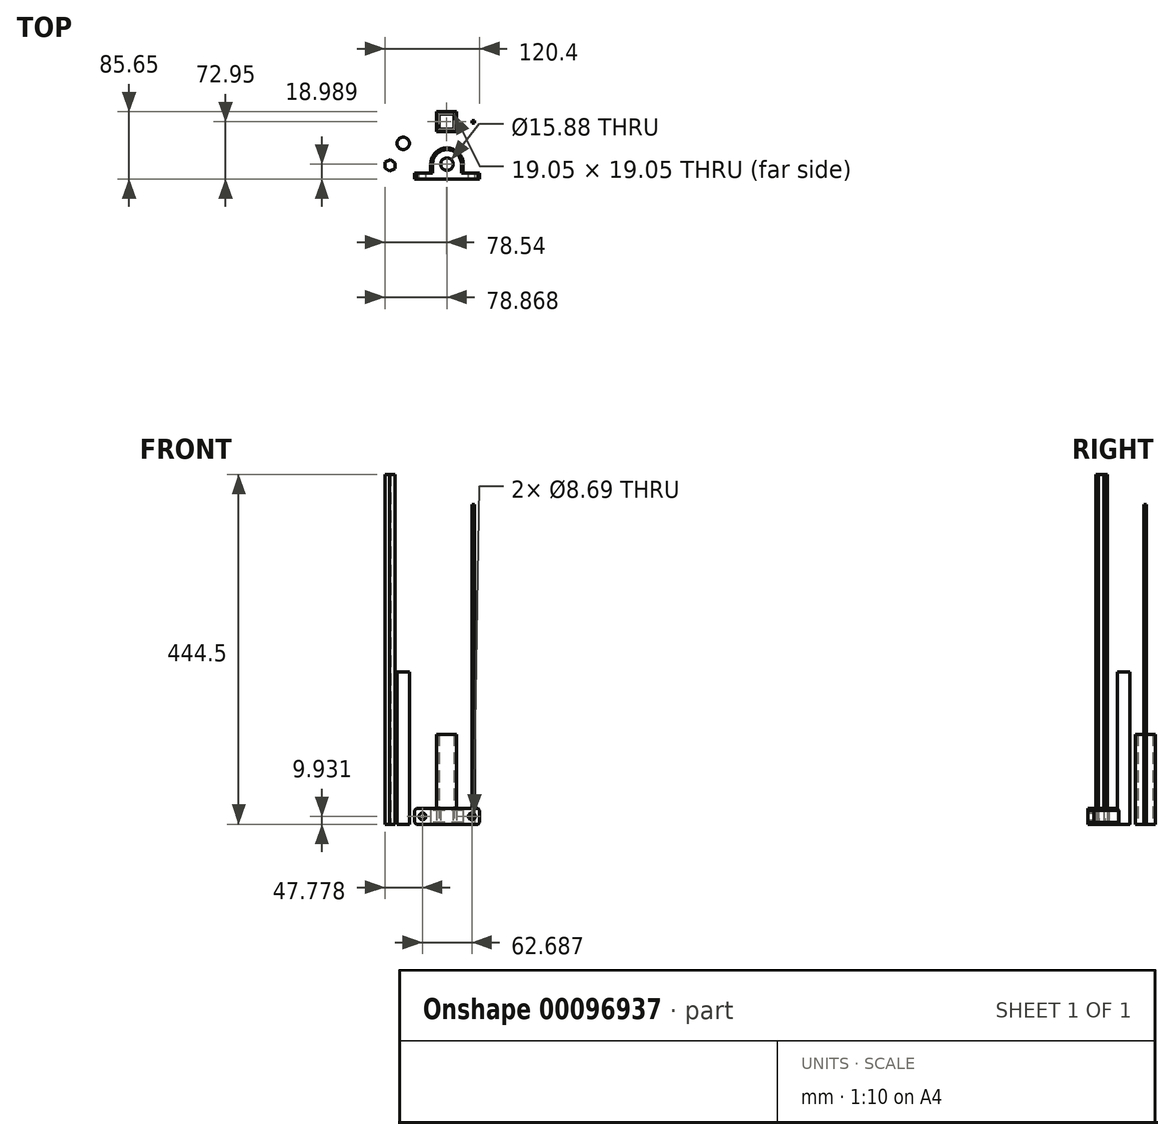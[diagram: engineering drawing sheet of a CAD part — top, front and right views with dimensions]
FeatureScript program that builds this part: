
annotation { "Feature Type Name" : "Feature", "Feature Type Description" : "" }
export const myFeature = defineFeature(function(context is Context, id is Id, definition is map)
    precondition{}
    {
        {
            var Q0;
            Q0=qCreatedBy(makeId("Top.planeOp"),FACE);
            var sketch = newSketch(context, id + "F0", { "sketchPlane" : qUnion([Q0])});
            skLineSegment(sketch, "E0.bottom", {"start": v(0, 0) * mm, "end": v(25.4, 0) * mm});
            skLineSegment(sketch, "E0.top", {"start": v(0, 25.4) * mm, "end": v(25.4, 25.4) * mm});
            skLineSegment(sketch, "E0.left", {"start": v(0, 0) * mm, "end": v(0, 25.4) * mm});
            skLineSegment(sketch, "E0.right", {"start": v(25.4, 0) * mm, "end": v(25.4, 25.4) * mm});
            skLineSegment(sketch, "E1.bottom", {"start": v(3.17, 3.18) * mm, "end": v(22.22, 3.18) * mm});
            skLineSegment(sketch, "E1.top", {"start": v(3.17, 22.23) * mm, "end": v(22.22, 22.23) * mm});
            skLineSegment(sketch, "E1.left", {"start": v(3.17, 3.18) * mm, "end": v(3.17, 22.23) * mm});
            skLineSegment(sketch, "E1.right", {"start": v(22.22, 3.18) * mm, "end": v(22.22, 22.23) * mm});
            skSolve(sketch);
        }
        {
            var Q0;
            Q0=makeQuery(id+"F0.imprint","IMPRINT",FACE,{"disambiguationData":[TD([[makeQuery(id+"F0.imprint","IMPRINT",EDGE,{"derivedFrom":sQuery(id+"F0.wireOp",EDGE,"E0.bottom")}),1.0]])]});
            extrude(context, id + "F1", {"entities" : qUnion([Q0]), "depth" : 114.3 * mm});
        }
        {
            var Q0;
            Q0=qCreatedBy(makeId("Top.planeOp"),FACE);
            var sketch = newSketch(context, id + "F2", { "sketchPlane" : qUnion([Q0])});
            skCircle(sketch, "E2", {"center": v(-42.54, -14.85) * mm, "radius": 7.94 * mm});
            skSolve(sketch);
        }
        {
            var Q0;
            Q0 = qSketchRegion(id + "F2", true);
            extrude(context, id + "F3", {"entities" : qUnion([Q0]), "depth" : 193.67 * mm});
        }
        {
            var Q0;
            Q0=qCreatedBy(makeId("Top.planeOp"),FACE);
            var sketch = newSketch(context, id + "F4", { "sketchPlane" : qUnion([Q0])});
            skLineSegment(sketch, "E3.bottom", {"start": v(-28, -60.25) * mm, "end": v(54.56, -60.25) * mm});
            skLineSegment(sketch, "E3.top", {"start": v(-28, -52.31) * mm, "end": v(-7.6, -52.31) * mm});
            skLineSegment(sketch, "E3.left", {"start": v(-28, -60.25) * mm, "end": v(-28, -52.31) * mm});
            skLineSegment(sketch, "E3.right", {"start": v(54.56, -60.25) * mm, "end": v(54.56, -52.31) * mm});
            skLineSegment(sketch, "E4.top", {"start": v(13.03, -20.62) * mm, "end": v(13.03, -20.62) * mm});
            skLineSegment(sketch, "E4.left", {"start": v(-7.6, -52.31) * mm, "end": v(-7.6, -41.26) * mm});
            skLineSegment(sketch, "E4.right", {"start": v(33.67, -52.31) * mm, "end": v(33.67, -41.26) * mm});
            skPoint(sketch, "E5.visualSharp", {"position": v(-7.6, -20.62) * mm});
            skArc(sketch, "E5.filletArc", {"start": v(13.03, -20.62) * mm, "mid": v(-1.57, -26.67) * mm, "end": v(-7.6, -41.26) * mm});
            skPoint(sketch, "E6.visualSharp", {"position": v(33.67, -20.62) * mm});
            skArc(sketch, "E6.filletArc", {"start": v(33.67, -41.26) * mm, "mid": v(27.62, -26.67) * mm, "end": v(13.03, -20.62) * mm});
            skCircle(sketch, "E7", {"center": v(13.03, -41.26) * mm, "radius": 7.94 * mm});
            skLineSegment(sketch, "E8.trimOffspring", {"start": v(33.67, -52.31) * mm, "end": v(54.56, -52.31) * mm});
            skSolve(sketch);
        }
        {
            var Q0;
            Q0=makeQuery(id+"F4.imprint","IMPRINT",FACE,{"disambiguationData":[TD([[makeQuery(id+"F4.imprint","IMPRINT",EDGE,{"derivedFrom":sQuery(id+"F4.wireOp",EDGE,"E3.bottom")}),1.0]])]});
            extrude(context, id + "F5", {"entities" : qUnion([Q0]), "depth" : 19.86 * mm});
        }
        {
            var Q0;
            Q0=makeQuery(id+"F5.opExtrude","CAP_EDGE",EDGE,{"disambiguationData":[OSD([sQuery(id+"F4.wireOp",EDGE,"E5.filletArc"),sQuery(id+"F4.wireOp",EDGE,"E6.filletArc")])],"isStart":false});
            var Q1;
            Q1=makeQuery(id+"F5.opExtrude","CAP_EDGE",EDGE,{"disambiguationData":[OSD([sQuery(id+"F4.wireOp",EDGE,"E4.left")])],"isStart":false});
            var Q2;
            Q2=makeQuery(id+"F5.opExtrude","CAP_EDGE",EDGE,{"disambiguationData":[OSD([sQuery(id+"F4.wireOp",EDGE,"E4.right")])],"isStart":false});
            var Q3;
            Q3=makeQuery(id+"F5.opExtrude","CAP_EDGE",EDGE,{"disambiguationData":[OSD([sQuery(id+"F4.wireOp",EDGE,"E4.right")])],"isStart":true});
            var Q4;
            Q4=makeQuery(id+"F5.opExtrude","CAP_EDGE",EDGE,{"disambiguationData":[OSD([sQuery(id+"F4.wireOp",EDGE,"E5.filletArc"),sQuery(id+"F4.wireOp",EDGE,"E6.filletArc")])],"isStart":true});
            var Q5;
            Q5=makeQuery(id+"F5.opExtrude","CAP_EDGE",EDGE,{"disambiguationData":[OSD([sQuery(id+"F4.wireOp",EDGE,"E4.left")])],"isStart":true});
            var Q6;
            Q6=makeQuery(id+"F5.opExtrude","CAP_EDGE",EDGE,{"disambiguationData":[OSD([sQuery(id+"F4.wireOp",EDGE,"E3.right")])],"isStart":true});
            var Q7;
            Q7=makeQuery(id+"F5.opExtrude","CAP_EDGE",EDGE,{"disambiguationData":[OSD([sQuery(id+"F4.wireOp",EDGE,"E3.right")])],"isStart":false});
            var Q8;
            Q8=makeQuery(id+"F5.opExtrude","CAP_EDGE",EDGE,{"disambiguationData":[OSD([sQuery(id+"F4.wireOp",EDGE,"E3.left")])],"isStart":true});
            var Q9;
            Q9=makeQuery(id+"F5.opExtrude","CAP_EDGE",EDGE,{"disambiguationData":[OSD([sQuery(id+"F4.wireOp",EDGE,"E3.left")])],"isStart":false});
            chamfer(context, id + "F6", {"entities" : qUnion([Q0, Q1, Q2, Q3, Q4, Q5, Q6, Q7, Q8, Q9]), "width" : 2.3 * mm, "tangentPropagation" : true});
        }
        {
            var Q0;
            Q0=makeQuery(id+"F5.opExtrude","SWEPT_FACE",FACE,{"disambiguationData":[OSD([sQuery(id+"F4.wireOp",EDGE,"E8.trimOffspring")])]});
            var sketch = newSketch(context, id + "F7", { "sketchPlane" : qUnion([Q0])});
            skCircle(sketch, "E9", {"center": v(18.06, 9.93) * mm, "radius": 4.34 * mm});
            skCircle(sketch, "E10", {"center": v(-44.63, 9.93) * mm, "radius": 4.34 * mm});
            skSolve(sketch);
        }
        {
            var Q0;
            Q0=makeQuery(id+"F7.imprint","IMPRINT",FACE,{"disambiguationData":[TD([[makeQuery(id+"F7.imprint","IMPRINT",EDGE,{"derivedFrom":sQuery(id+"F7.wireOp",EDGE,"E10")}),1.0]])]});
            var Q1;
            Q1=makeQuery(id+"F7.imprint","IMPRINT",FACE,{"disambiguationData":[TD([[makeQuery(id+"F7.imprint","IMPRINT",EDGE,{"derivedFrom":sQuery(id+"F7.wireOp",EDGE,"E9")}),1.0]])]});
            extrude(context, id + "F8", {"entities" : qUnion([Q0, Q1]), "operationType" : NewBodyOperationType.REMOVE, "oppositeDirection" : true, "depth" : 25.4 * mm});
        }
        {
            var Q0;
            Q0=qCreatedBy(makeId("Top.planeOp"),FACE);
            var sketch = newSketch(context, id + "F9", { "sketchPlane" : qUnion([Q0])});
            skCircle(sketch, "E11.cCircle", {"center": v(-59.3, -42.92) * mm, "radius": 6.35 * mm, "construction": true});
            skLineSegment(sketch, "E11.0", {"start": v(-58.88, -35.6) * mm, "end": v(-52.75, -39.62) * mm});
            skLineSegment(sketch, "E11.1", {"start": v(-52.75, -39.62) * mm, "end": v(-53.16, -46.94) * mm});
            skLineSegment(sketch, "E11.2", {"start": v(-53.16, -46.94) * mm, "end": v(-59.7, -50.24) * mm});
            skLineSegment(sketch, "E11.3", {"start": v(-59.7, -50.24) * mm, "end": v(-65.84, -46.22) * mm});
            skLineSegment(sketch, "E11.4", {"start": v(-65.84, -46.22) * mm, "end": v(-65.43, -38.9) * mm});
            skLineSegment(sketch, "E11.5", {"start": v(-65.43, -38.9) * mm, "end": v(-58.88, -35.6) * mm});
            skPoint(sketch, "E11.0.midPoint", {"position": v(-55.81, -37.6) * mm});
            skSolve(sketch);
        }
        {
            var Q0;
            Q0=makeQuery(id+"F9.imprint","IMPRINT",FACE,{"disambiguationData":[TD([[makeQuery(id+"F9.imprint","IMPRINT",EDGE,{"derivedFrom":sQuery(id+"F9.wireOp",EDGE,"E11.0")}),-1.0]])]});
            extrude(context, id + "F10", {"entities" : qUnion([Q0]), "depth" : 444.5 * mm});
        }
        {
            var Q0;
            Q0=qCreatedBy(makeId("Top.planeOp"),FACE);
            var sketch = newSketch(context, id + "F11", { "sketchPlane" : qUnion([Q0])});
            skLineSegment(sketch, "E12.bottom", {"start": v(44.64, 14.3) * mm, "end": v(47.81, 14.3) * mm});
            skLineSegment(sketch, "E12.top", {"start": v(44.64, 11.13) * mm, "end": v(47.81, 11.13) * mm});
            skLineSegment(sketch, "E12.left", {"start": v(44.64, 14.3) * mm, "end": v(44.64, 11.13) * mm});
            skLineSegment(sketch, "E12.right", {"start": v(47.81, 14.3) * mm, "end": v(47.81, 11.13) * mm});
            skSolve(sketch);
        }
        {
            var Q0;
            Q0=makeQuery(id+"F11.imprint","IMPRINT",FACE,{"disambiguationData":[TD([[makeQuery(id+"F11.imprint","IMPRINT",EDGE,{"derivedFrom":sQuery(id+"F11.wireOp",EDGE,"E12.bottom")}),-1.0]])]});
            extrude(context, id + "F12", {"entities" : qUnion([Q0]), "depth" : 406.4 * mm});
        }
    });
